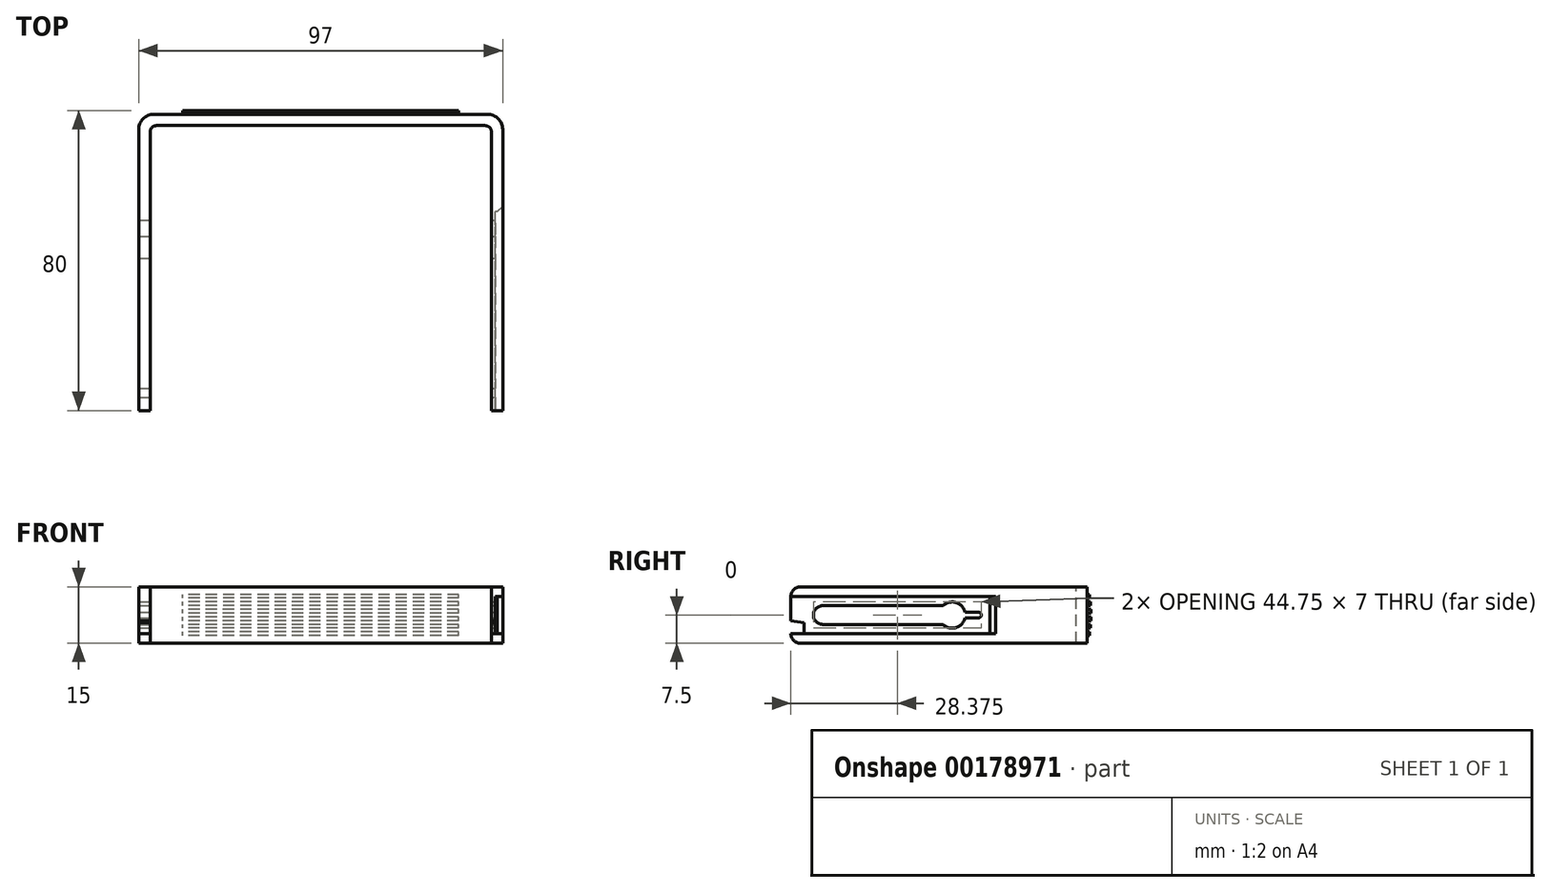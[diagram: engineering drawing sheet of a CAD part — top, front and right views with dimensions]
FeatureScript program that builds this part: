
annotation { "Feature Type Name" : "Feature", "Feature Type Description" : "" }
export const myFeature = defineFeature(function(context is Context, id is Id, definition is map)
    precondition{}
    {
        {
            var Q0;
            Q0=qCreatedBy(makeId("Top.planeOp"),FACE);
            var sketch = newSketch(context, id + "F0", { "sketchPlane" : qUnion([Q0])});
            skLineSegment(sketch, "E0", {"start": v(-48.5, 0) * mm, "end": v(48.5, 0) * mm});
            skLineSegment(sketch, "E1", {"start": v(-48.5, 0) * mm, "end": v(-48.5, -79) * mm});
            skLineSegment(sketch, "E2", {"start": v(-48.5, -79) * mm, "end": v(-45.5, -79) * mm});
            skLineSegment(sketch, "E3", {"start": v(-45.5, 0) * mm, "end": v(-45.5, -3) * mm, "construction": true});
            skLineSegment(sketch, "E4", {"start": v(-45.5, -79) * mm, "end": v(-45.5, -3) * mm});
            skLineSegment(sketch, "E5", {"start": v(0, 0) * mm, "end": v(0, -36.64) * mm, "construction": true});
            skLineSegment(sketch, "E6.MirrorCS", {"start": v(45.5, -79) * mm, "end": v(45.5, -3) * mm});
            skLineSegment(sketch, "E7.MirrorCS", {"start": v(48.5, 0) * mm, "end": v(48.5, -79) * mm});
            skLineSegment(sketch, "E8.MirrorCS", {"start": v(48.5, -79) * mm, "end": v(45.5, -79) * mm});
            skLineSegment(sketch, "E9", {"start": v(-45.5, -3) * mm, "end": v(45.5, -3) * mm});
            skLineSegment(sketch, "E10.MirrorCS", {"start": v(49, -24) * mm, "end": v(47, -26) * mm});
            skLineSegment(sketch, "E11.MirrorCS", {"start": v(47, -26) * mm, "end": v(49, -26) * mm});
            skSolve(sketch);
        }
        {
            var Q0;
            Q0=qCreatedBy(makeId("Right.planeOp"),FACE);
            var sketch = newSketch(context, id + "F1", { "sketchPlane" : qUnion([Q0])});
            skLineSegment(sketch, "E12", {"start": v(0, 0) * mm, "end": v(-79, 0) * mm});
            skLineSegment(sketch, "E13", {"start": v(-79, 0) * mm, "end": v(-79, 2.5) * mm});
            skLineSegment(sketch, "E14", {"start": v(0, 0) * mm, "end": v(0, 15) * mm});
            skLineSegment(sketch, "E15", {"start": v(0, 7.5) * mm, "end": v(-24, 7.5) * mm, "construction": true});
            skLineSegment(sketch, "E16", {"start": v(-79, 2.5) * mm, "end": v(-24, 2.5) * mm});
            skLineSegment(sketch, "E17", {"start": v(-24, 2.5) * mm, "end": v(-24, 7.5) * mm});
            skLineSegment(sketch, "E18.MirrorCS", {"start": v(-24, 12.5) * mm, "end": v(-24, 7.5) * mm});
            skLineSegment(sketch, "E19.MirrorCS", {"start": v(-79, 12.5) * mm, "end": v(-24, 12.5) * mm});
            skLineSegment(sketch, "E20.MirrorCS", {"start": v(-79, 15) * mm, "end": v(-79, 12.5) * mm});
            skLineSegment(sketch, "E21.MirrorCS", {"start": v(0, 15) * mm, "end": v(-79, 15) * mm});
            skLineSegment(sketch, "E22", {"start": v(-79, 2.5) * mm, "end": v(-79, 7.5) * mm});
            skLineSegment(sketch, "E23.MirrorCS", {"start": v(-79, 12.5) * mm, "end": v(-79, 7.5) * mm});
            skCircle(sketch, "E24", {"center": v(-36, 7.5) * mm, "radius": 3.5 * mm});
            skLineSegment(sketch, "E25", {"start": v(-24, 7.5) * mm, "end": v(-36, 7.5) * mm, "construction": true});
            skLineSegment(sketch, "E26", {"start": v(-79, 7.5) * mm, "end": v(-70.5, 7.5) * mm, "construction": true});
            skCircle(sketch, "E27", {"center": v(-70.5, 7.5) * mm, "radius": 2.5 * mm});
            skLineSegment(sketch, "E28", {"start": v(-70.5, 5) * mm, "end": v(-38.45, 5) * mm});
            skLineSegment(sketch, "E29.MirrorCS", {"start": v(-70.5, 10) * mm, "end": v(-38.45, 10) * mm});
            skLineSegment(sketch, "E30", {"start": v(-26, 2.5) * mm, "end": v(-26, 12.5) * mm});
            skLineSegment(sketch, "E31", {"start": v(-79, 6) * mm, "end": v(-75.5, 5.5) * mm});
            skLineSegment(sketch, "E32", {"start": v(-75.5, 5.5) * mm, "end": v(-75.5, 2.5) * mm});
            skCircle(sketch, "E33", {"center": v(-29, 7.5) * mm, "radius": 0.75 * mm});
            skLineSegment(sketch, "E34", {"start": v(-29, 6.75) * mm, "end": v(-32.58, 6.75) * mm});
            skLineSegment(sketch, "E35.MirrorCS", {"start": v(-29, 8.25) * mm, "end": v(-32.58, 8.25) * mm});
            skSolve(sketch);
        }
        {
            var Q0;
            Q0=qCreatedBy(makeId("Front.planeOp"),FACE);
            var sketch = newSketch(context, id + "F2", { "sketchPlane" : qUnion([Q0])});
            skLineSegment(sketch, "E36", {"start": v(38.5, 0) * mm, "end": v(-38.5, 0) * mm});
            skLineSegment(sketch, "E37", {"start": v(38.5, 0) * mm, "end": v(38.5, 15) * mm});
            skLineSegment(sketch, "E38", {"start": v(38.5, 15) * mm, "end": v(-38.5, 15) * mm});
            skLineSegment(sketch, "E39", {"start": v(-38.5, 15) * mm, "end": v(-38.5, 0) * mm});
            skLineSegment(sketch, "E40", {"start": v(0, 0) * mm, "end": v(0, 15) * mm, "construction": true});
            skLineSegment(sketch, "E41", {"start": v(38.5, 7.5) * mm, "end": v(-38.5, 7.5) * mm, "construction": true});
            skLineSegment(sketch, "E42.0.2.0", {"start": v(36.75, 13) * mm, "end": v(-36.75, 13) * mm});
            skLineSegment(sketch, "E42.0.2.1", {"start": v(36.75, 12) * mm, "end": v(36.75, 13) * mm});
            skLineSegment(sketch, "E42.0.2.2", {"start": v(36.75, 12) * mm, "end": v(-36.75, 12) * mm});
            skLineSegment(sketch, "E42.0.2.3", {"start": v(-36.75, 12) * mm, "end": v(-36.75, 13) * mm});
            skLineSegment(sketch, "E43.0.1.0", {"start": v(36.74, 11) * mm, "end": v(-36.76, 11) * mm});
            skLineSegment(sketch, "E43.0.1.1", {"start": v(36.74, 10) * mm, "end": v(-36.76, 10) * mm});
            skLineSegment(sketch, "E43.0.1.2", {"start": v(36.74, 10) * mm, "end": v(36.74, 11) * mm});
            skLineSegment(sketch, "E43.0.1.3", {"start": v(-36.76, 10) * mm, "end": v(-36.76, 11) * mm});
            skLineSegment(sketch, "E43.0.2.0", {"start": v(36.73, 9) * mm, "end": v(-36.77, 9) * mm});
            skLineSegment(sketch, "E43.0.2.1", {"start": v(36.73, 8) * mm, "end": v(-36.77, 8) * mm});
            skLineSegment(sketch, "E43.0.2.2", {"start": v(36.73, 8) * mm, "end": v(36.73, 9) * mm});
            skLineSegment(sketch, "E43.0.2.3", {"start": v(-36.77, 8) * mm, "end": v(-36.77, 9) * mm});
            skLineSegment(sketch, "E43.0.3.0", {"start": v(36.72, 7) * mm, "end": v(-36.78, 7) * mm});
            skLineSegment(sketch, "E43.0.3.1", {"start": v(36.72, 6) * mm, "end": v(-36.78, 6) * mm});
            skLineSegment(sketch, "E43.0.3.2", {"start": v(36.72, 6) * mm, "end": v(36.72, 7) * mm});
            skLineSegment(sketch, "E43.0.3.3", {"start": v(-36.78, 6) * mm, "end": v(-36.78, 7) * mm});
            skLineSegment(sketch, "E43.0.4.0", {"start": v(36.7, 5) * mm, "end": v(-36.8, 5) * mm});
            skLineSegment(sketch, "E43.0.4.1", {"start": v(36.7, 4) * mm, "end": v(-36.8, 4) * mm});
            skLineSegment(sketch, "E43.0.4.2", {"start": v(36.7, 4) * mm, "end": v(36.7, 5) * mm});
            skLineSegment(sketch, "E43.0.4.3", {"start": v(-36.8, 4) * mm, "end": v(-36.8, 5) * mm});
            skLineSegment(sketch, "E43.0.5.0", {"start": v(36.7, 3) * mm, "end": v(-36.8, 3) * mm});
            skLineSegment(sketch, "E43.0.5.1", {"start": v(36.7, 2) * mm, "end": v(-36.8, 2) * mm});
            skLineSegment(sketch, "E43.0.5.2", {"start": v(36.7, 2) * mm, "end": v(36.7, 3) * mm});
            skLineSegment(sketch, "E43.0.5.3", {"start": v(-36.8, 2) * mm, "end": v(-36.8, 3) * mm});
            skLineSegment(sketch, "E43.direction1", {"start": v(-36.75, 12) * mm, "end": v(-11.75, 12) * mm, "construction": true});
            skLineSegment(sketch, "E43.direction2", {"start": v(-36.75, 12) * mm, "end": v(-36.76, 10) * mm, "construction": true});
            skSolve(sketch);
        }
        {
            var Q0;
            {var subQ3=sQuery(id+"F0.wireOp",EDGE,"E0");Q0=makeQuery(id+"F0.imprint","IMPRINT",FACE,{"disambiguationData":[TD([[makeQuery(id+"F0.imprint","IMPRINT",EDGE,{"derivedFrom":subQ3}),-1.0]])]});}
            var Q1;
            {var subQ0=sQuery(id+"F0.wireOp",EDGE,"E10.MirrorCS");Q1=makeQuery(id+"F0.imprint","IMPRINT",FACE,{"disambiguationData":[TD([[makeQuery(id+"F0.imprint","IMPRINT",EDGE,{"derivedFrom":subQ0}),1.0]])]});}
            extrude(context, id + "F3", {"entities" : qUnion([Q0, Q1]), "depth" : 15 * mm});
        }
        {
            var Q0;
            Q0=makeQuery(id+"F3.opExtrude","CAP_EDGE",EDGE,{"disambiguationData":[OSD([sQuery(id+"F0.wireOp",EDGE,"E2")])],"isStart":false});
            var Q1;
            Q1=makeQuery(id+"F3.opExtrude","CAP_EDGE",EDGE,{"disambiguationData":[OSD([sQuery(id+"F0.wireOp",EDGE,"E2")])],"isStart":true});
            var Q2;
            Q2=makeQuery(id+"F3.opExtrude","CAP_EDGE",EDGE,{"disambiguationData":[OSD([sQuery(id+"F0.wireOp",EDGE,"E8.MirrorCS")])],"isStart":true});
            var Q3;
            Q3=makeQuery(id+"F3.opExtrude","CAP_EDGE",EDGE,{"disambiguationData":[OSD([sQuery(id+"F0.wireOp",EDGE,"E8.MirrorCS")])],"isStart":false});
            fillet(context, id + "F4", {"entities" : qUnion([Q0, Q1, Q2, Q3]), "radius" : 2.5 * mm, "tangentPropagation" : true, "allowEdgeOverflow" : false});
        }
        {
            var Q0;
            {var subQ0=sQuery(id+"F1.wireOp",EDGE,"E28");Q0=makeQuery(id+"F1.imprint","IMPRINT",FACE,{"disambiguationData":[TD([[makeQuery(id+"F1.imprint","IMPRINT",EDGE,{"derivedFrom":subQ0}),1.0]])]});}
            var Q1;
            {var subQ0=sQuery(id+"F1.wireOp",EDGE,"E27");var subQ1=makeQuery(id+"F1.imprint","INTERSECT",VERTEX,{"derivedFrom":[subQ0,sQuery(id+"F1.wireOp",EDGE,"E28")]});Q1=makeQuery(id+"F1.imprint","IMPRINT",FACE,{"disambiguationData":[TD([[makeQuery(id+"F1.imprint","IMPRINT",EDGE,{"disambiguationData":[TD([[subQ1,1.0]])],"derivedFrom":subQ0}),1.0]])]});}
            var Q2;
            {var subQ0=sQuery(id+"F1.wireOp",EDGE,"E24");var subQ1=makeQuery(id+"F1.imprint","INTERSECT",VERTEX,{"derivedFrom":[subQ0,sQuery(id+"F1.wireOp",EDGE,"E28")]});Q2=makeQuery(id+"F1.imprint","IMPRINT",FACE,{"disambiguationData":[TD([[makeQuery(id+"F1.imprint","IMPRINT",EDGE,{"disambiguationData":[TD([[subQ1,1.0]])],"derivedFrom":subQ0}),1.0]])]});}
            var Q3;
            {var subQ4=sQuery(id+"F1.wireOp",EDGE,"E31");Q3=makeQuery(id+"F1.imprint","IMPRINT",FACE,{"disambiguationData":[TD([[makeQuery(id+"F1.imprint","IMPRINT",EDGE,{"derivedFrom":subQ4}),-1.0]])]});}
            var Q4;
            {var subQ0=sQuery(id+"F1.wireOp",EDGE,"E34");Q4=makeQuery(id+"F1.imprint","IMPRINT",FACE,{"disambiguationData":[TD([[makeQuery(id+"F1.imprint","IMPRINT",EDGE,{"derivedFrom":subQ0}),-1.0]])]});}
            var Q5;
            {var subQ0=sQuery(id+"F1.wireOp",EDGE,"E33");var subQ1=makeQuery(id+"F1.imprint","INTERSECT",VERTEX,{"derivedFrom":[subQ0,sQuery(id+"F1.wireOp",EDGE,"E34")]});Q5=makeQuery(id+"F1.imprint","IMPRINT",FACE,{"disambiguationData":[TD([[makeQuery(id+"F1.imprint","IMPRINT",EDGE,{"disambiguationData":[TD([[subQ1,1.0]])],"derivedFrom":subQ0}),1.0]])]});}
            extrude(context, id + "F5", {"entities" : qUnion([Q0, Q1, Q2, Q3, Q4, Q5]), "operationType" : NewBodyOperationType.REMOVE, "endBound" : BoundingType.THROUGH_ALL, "oppositeDirection" : true, "depth" : 25 * mm, "hasSecondDirection" : true, "secondDirectionBound" : SecondDirectionBoundingType.THROUGH_ALL, "secondDirectionOppositeDirection" : false, "secondDirectionDepth" : 25 * mm});
        }
        {
            var Q0;
            {var subQ4=sQuery(id+"F1.wireOp",EDGE,"E31");Q0=makeQuery(id+"F1.imprint","IMPRINT",FACE,{"disambiguationData":[TD([[makeQuery(id+"F1.imprint","IMPRINT",EDGE,{"derivedFrom":subQ4}),-1.0]])]});}
            var Q1;
            {var subQ2=sQuery(id+"F1.wireOp",EDGE,"E23.MirrorCS");Q1=makeQuery(id+"F1.imprint","IMPRINT",FACE,{"disambiguationData":[TD([[makeQuery(id+"F1.imprint","IMPRINT",EDGE,{"derivedFrom":subQ2}),1.0]])]});}
            var Q2;
            {var subQ0=sQuery(id+"F1.wireOp",EDGE,"E28");Q2=makeQuery(id+"F1.imprint","IMPRINT",FACE,{"disambiguationData":[TD([[makeQuery(id+"F1.imprint","IMPRINT",EDGE,{"derivedFrom":subQ0}),1.0]])]});}
            var Q3;
            {var subQ0=sQuery(id+"F1.wireOp",EDGE,"E27");var subQ1=makeQuery(id+"F1.imprint","INTERSECT",VERTEX,{"derivedFrom":[subQ0,sQuery(id+"F1.wireOp",EDGE,"E28")]});Q3=makeQuery(id+"F1.imprint","IMPRINT",FACE,{"disambiguationData":[TD([[makeQuery(id+"F1.imprint","IMPRINT",EDGE,{"disambiguationData":[TD([[subQ1,1.0]])],"derivedFrom":subQ0}),1.0]])]});}
            var Q4;
            {var subQ0=sQuery(id+"F1.wireOp",EDGE,"E24");var subQ1=makeQuery(id+"F1.imprint","INTERSECT",VERTEX,{"derivedFrom":[subQ0,sQuery(id+"F1.wireOp",EDGE,"E28")]});Q4=makeQuery(id+"F1.imprint","IMPRINT",FACE,{"disambiguationData":[TD([[makeQuery(id+"F1.imprint","IMPRINT",EDGE,{"disambiguationData":[TD([[subQ1,1.0]])],"derivedFrom":subQ0}),1.0]])]});}
            extrude(context, id + "F6", {"entities" : qUnion([Q0, Q1, Q2, Q3, Q4]), "operationType" : NewBodyOperationType.REMOVE, "depth" : 55 * mm, "hasSecondDirection" : true, "secondDirectionOppositeDirection" : false, "secondDirectionDepth" : 46.5 * mm});
        }
        {
            var Q0;
            {var subQ0=sQuery(id+"F0.wireOp",EDGE,"E10.MirrorCS");Q0=makeQuery(id+"F0.imprint","IMPRINT",FACE,{"disambiguationData":[TD([[makeQuery(id+"F0.imprint","IMPRINT",EDGE,{"derivedFrom":subQ0}),1.0]])]});}
            extrude(context, id + "F7", {"entities" : qUnion([Q0]), "operationType" : NewBodyOperationType.REMOVE, "depth" : 12.5 * mm, "hasSecondDirection" : true, "secondDirectionOppositeDirection" : false, "secondDirectionDepth" : 2.5 * mm});
        }
        {
            var Q0;
            Q0=makeQuery(id+"F2.imprint","IMPRINT",FACE,{"disambiguationData":[TD([[makeQuery(id+"F2.imprint","IMPRINT",EDGE,{"derivedFrom":sQuery(id+"F2.wireOp",EDGE,"E42.0.2.0")}),1.0]])]});
            var Q1;
            Q1=makeQuery(id+"F2.imprint","IMPRINT",FACE,{"disambiguationData":[TD([[makeQuery(id+"F2.imprint","IMPRINT",EDGE,{"derivedFrom":sQuery(id+"F2.wireOp",EDGE,"E43.0.5.0")}),1.0]])]});
            extrude(context, id + "F8", {"entities" : qUnion([Q0, Q1]), "operationType" : NewBodyOperationType.ADD, "oppositeDirection" : true, "depth" : 0.6 * mm});
        }
        {
            var Q0;
            Q0=makeQuery(id+"F2.imprint","IMPRINT",FACE,{"disambiguationData":[TD([[makeQuery(id+"F2.imprint","IMPRINT",EDGE,{"derivedFrom":sQuery(id+"F2.wireOp",EDGE,"E43.0.1.0")}),1.0]])]});
            var Q1;
            Q1=makeQuery(id+"F2.imprint","IMPRINT",FACE,{"disambiguationData":[TD([[makeQuery(id+"F2.imprint","IMPRINT",EDGE,{"derivedFrom":sQuery(id+"F2.wireOp",EDGE,"E43.0.4.0")}),1.0]])]});
            extrude(context, id + "F9", {"entities" : qUnion([Q0, Q1]), "operationType" : NewBodyOperationType.ADD, "oppositeDirection" : true, "depth" : 0.8 * mm});
        }
        {
            var Q0;
            Q0=makeQuery(id+"F2.imprint","IMPRINT",FACE,{"disambiguationData":[TD([[makeQuery(id+"F2.imprint","IMPRINT",EDGE,{"derivedFrom":sQuery(id+"F2.wireOp",EDGE,"E43.0.2.0")}),1.0]])]});
            var Q1;
            Q1=makeQuery(id+"F2.imprint","IMPRINT",FACE,{"disambiguationData":[TD([[makeQuery(id+"F2.imprint","IMPRINT",EDGE,{"derivedFrom":sQuery(id+"F2.wireOp",EDGE,"E43.0.3.0")}),1.0]])]});
            extrude(context, id + "F10", {"entities" : qUnion([Q0, Q1]), "operationType" : NewBodyOperationType.ADD, "oppositeDirection" : true, "depth" : 1 * mm});
        }
        {
            var Q0;
            Q0=makeQuery(id+"F3.opExtrude","SWEPT_EDGE",EDGE,{"disambiguationData":[OSD([sQuery(id+"F0.wireOp",EDGE,"E0"),sQuery(id+"F0.wireOp",EDGE,"E7.MirrorCS")])]});
            var Q1;
            Q1=makeQuery(id+"F3.opExtrude","SWEPT_EDGE",EDGE,{"disambiguationData":[OSD([sQuery(id+"F0.wireOp",EDGE,"E0"),sQuery(id+"F0.wireOp",EDGE,"E1")])]});
            fillet(context, id + "F11", {"entities" : qUnion([Q0, Q1]), "radius" : 4 * mm, "allowEdgeOverflow" : false});
        }
        {
            var Q0;
            Q0=makeQuery(id+"F3.opExtrude","SWEPT_EDGE",EDGE,{"disambiguationData":[OSD([sQuery(id+"F0.wireOp",EDGE,"E4"),sQuery(id+"F0.wireOp",EDGE,"E9")])]});
            var Q1;
            Q1=makeQuery(id+"F3.opExtrude","SWEPT_EDGE",EDGE,{"disambiguationData":[OSD([sQuery(id+"F0.wireOp",EDGE,"E6.MirrorCS"),sQuery(id+"F0.wireOp",EDGE,"E9")])]});
            fillet(context, id + "F12", {"entities" : qUnion([Q0, Q1]), "radius" : 2 * mm, "rho" : 0.5, "crossSection" : FilletCrossSection.CONIC, "allowEdgeOverflow" : false});
        }
    });
